# Revit family: O41 LED 2000 HF 830 WB BLACK_Unhosted
name_source: partatom
category: Lighting Fixtures
revit_build: Autodesk Revit 2016 (Build: 20151007_0715(x64)
units: mm (PartAtom-declared; Revit-internal decimal feet)

## family parameters
Always vertical = Yes
Cut with Voids When Loaded = No
Light Source = Yes
OmniClass Number = 23.80.70.00
OmniClass Title = Lighting
Part Type = Normal
Room Calculation Point = No
Round Connector Dimension = Use Diameter
Shared = No
Work Plane-Based = No

## types (1)
- O41 LED 2000 HF 830 WB BLACK_Unhosted
    # ballast on a MCB16 type B fuse = 28
    # ballast on a MCB16 type C fuse = 47
    #Ballast = 1
    Apparent Load = 22 VA
    ArticleNumber = O418208312
    Body Material and Colour = Default
    Color Filter = 16777215
    Description = O41 LED 2000 HF 830 WB BLACK
    Diameter = 520 mm  [stored 1.70604 ft]
    Diameter1 = 0 mm  [stored 0 ft]
    Dimming Lamp Color Temperature Shift = Incandescent Lamp Curve
    EANNo = 8054378360497
    Emit Shape Visible in Rendering = Yes
    Emit from Circle Diameter = 145 mm  [stored 0.475722 ft]
    Expired = 0
    Frequency = 50 Hz
    FrequencyMax = 60 Hz
    Glamox Category = Outdoor
    Glamox Family = O41
    Glamox Mounting = Pole
    GlobalTradeItemNumber = 8054378360497
    Height = 675 mm  [stored 2.21457 ft]
    IFC Classification = Light Fixture
    IPClass = 66
    IP_Code = 66
    Lamp = LED
    LightFixtureMountingType = POLE_TOP
    LightFixturePlacingType = POLE
    LumDiameter = 145 mm  [stored 0.475722 ft]
    MFArtNo = O418208312
    MaintenanceFactor = 0
    Manufacturer = Glamox
    Maximum TA = 45
    ModelLabel = O41 LED 2000 HF 830 WB BLACK
    ModelReference = O41
    NominalFrequencyRange = 50 Hz
    Number of Poles = 1
    Optic = WB
    Photometric Web File = O41-LED-2000-830-WB.ies
    Pole Radius = -15 mm  [stored -0.0492126 ft]
    Power Factor = 0.98
    PowerFactor = 98.00%
    Radius = 0 mm  [stored 0 ft]
    RatedVoltage = 220 V
    Specification = Outdoor product, in Aluminium, for Facade/Pole mounting, impact classification IK8, IP66, light source LED, lumen out 2000lm, ballast type HF = High frequency, with light source type CRI>80, 3000K, 6 metre cable, optic type WB = Wide Beam Reflector.
    Tilt Angle = 90.00°
    Total Load = 22 W
    TotalWattage = 22 W
    TypeOfBallast = HF = High frequency
    URL Denmark = http://glamox.com
    URL Estonia = http://glamox.com
    URL Finland = http://glamox.com
    URL Germany = http://glamox.com
    URL Ireland = http://glamox.com
    URL Norway = http://glamox.com
    URL Other = http://glamox.com
    URL Russia = http://glamox.com
    URL Sweden = http://glamox.com
    URL UK = http://glamox.com
    UpdateDate = 25.11.2020 14:30:45
    Voltage = 220 V
    VoltageMax = 240 V

note: [stored X ft] marks values corroborated as IEEE doubles in the binary element streams (Revit-internal decimal feet)

## geometry (parser evidence)
native form markers: Blend x4, Sweep x1
no freeform markers — native parametric forms only
